# Revit family: Betty Bench TK4
name_source: partatom
category: Furniture
revit_build: Autodesk Revit 2017 (Build: 20171027_0315(x64)
units: mm (PartAtom-declared; Revit-internal decimal feet)

## family parameters
Always vertical = Yes
Cut with Voids When Loaded = No
OmniClass Number = 23.40.20.00
OmniClass Title = General Furniture and Specialties
Room Calculation Point = No
Shared = No
Work Plane-Based = No

## types (1)
- Betty Bench TK4
    Depth = 36cm/14.2in
    Design = Thau & Kallio
    Design Year = 2019
    Frame horizontal = &tradition Lacquered Oak Black Matt Horizontal
    Frame vertical = &tradition Lacquered Oak Black Matt Vertical
    Height = 46cm/18.1
    Manufacturer = &tradition
    Model = Betty Bench TK4
    Packaging Dimensions = H:9cm / 3.5in x W:108cm / 42.5in x D:39cm / 15.4in
    Seat Webbing 01 = &tradition Natural linen webbing Horizontal
    Seat Webbing 02 = &tradition Natural linen webbing Vertical
    Type Comments = Betty Series
    URL = https://www.andtradition.com
    Variation 1 = Lacquered Maroon Oak w. linen natural webbing
    Variation 2 = Lacquered Twilight Oak w. linen natural webbing
    Weight = 5.8kg
    Width = 105cm/41.3in

## geometry (parser evidence)
native form markers: Sweep x2
no freeform markers — native parametric forms only
